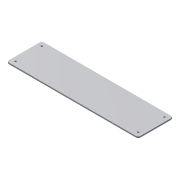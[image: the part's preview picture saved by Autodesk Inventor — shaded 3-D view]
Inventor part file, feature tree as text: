
AUTODESK INVENTOR PART (.ipt)
format: ipt  version: 2014 (Build 180170000, 170)  size: 97,280 bytes
history: native  units: mm
features: extrude x2, sketch x2, fillet x1
ambient origin geometry x8: Origin, YZ Plane, XZ Plane, XY Plane, X Axis, Y Axis, Z Axis, Center Point
bodies: Solid1 (feature_tree)
feature tree (5):
  extrude  "Extrusion1"  Depth=100.0mm
  extrude  "Extrusion8"  Depth=6.0mm
  fillet  "Fillet3"  Radius=10.0mm
  sketch  "Sketch1"  dims[d0=375.0mm d1=100.0mm]
  sketch  "Sketch8"  dims[d2=4.0mm d3=0.0mm d30=6.0mm d38=10.0mm d39=0.0mm d40=12.5mm d41=12.5mm d42=12.5mm d43=12.5mm d44=5.4mm]
